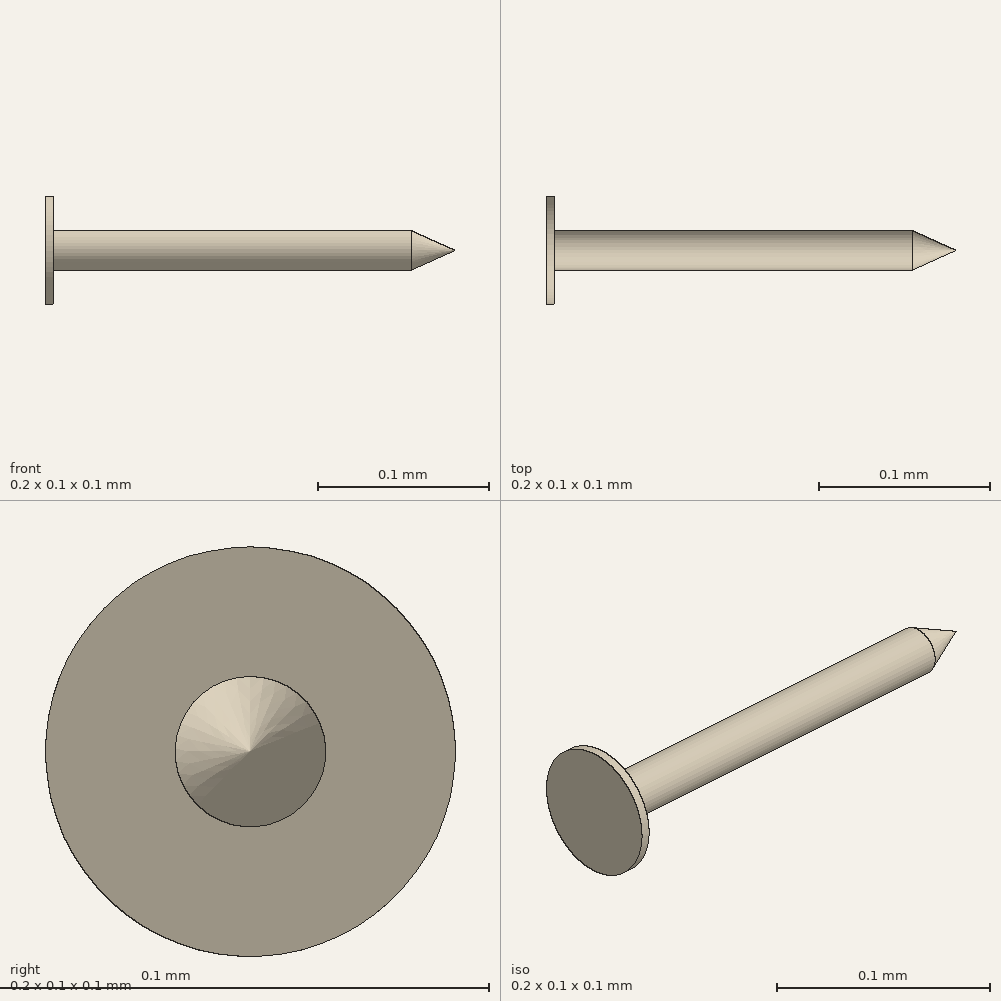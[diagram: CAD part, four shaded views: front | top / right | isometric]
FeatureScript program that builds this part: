
annotation { "Feature Type Name" : "Feature", "Feature Type Description" : "" }
export const myFeature = defineFeature(function(context is Context, id is Id, definition is map)
    precondition{}
    {
        {
            var Q0;
            Q0=qCreatedBy(makeId("Front.planeOp"),FACE);
            var sketch = newSketch(context, id + "F0", { "sketchPlane" : qUnion([Q0])});
            skLineSegment(sketch, "E0.bottom", {"start": v(-33.87, 35.93) * mm, "end": v(-33.66, 35.93) * mm});
            skLineSegment(sketch, "E0.top", {"start": v(-33.87, 35.92) * mm, "end": v(-33.66, 35.92) * mm});
            skLineSegment(sketch, "E0.left", {"start": v(-33.87, 35.93) * mm, "end": v(-33.87, 35.92) * mm});
            skLineSegment(sketch, "E0.right", {"start": v(-33.66, 35.93) * mm, "end": v(-33.66, 35.92) * mm});
            skLineSegment(sketch, "E1", {"start": v(-33.66, 35.93) * mm, "end": v(-33.64, 35.92) * mm});
            skLineSegment(sketch, "E2", {"start": v(-33.64, 35.92) * mm, "end": v(-33.66, 35.92) * mm});
            skLineSegment(sketch, "E3.bottom", {"start": v(-33.87, 35.92) * mm, "end": v(-33.88, 35.92) * mm});
            skLineSegment(sketch, "E3.top", {"start": v(-33.87, 35.95) * mm, "end": v(-33.88, 35.95) * mm});
            skLineSegment(sketch, "E3.left", {"start": v(-33.87, 35.92) * mm, "end": v(-33.87, 35.95) * mm});
            skLineSegment(sketch, "E3.right", {"start": v(-33.88, 35.92) * mm, "end": v(-33.88, 35.95) * mm});
            skSolve(sketch);
        }
        {
            var Q0;
            {var subQ3=sQuery(id+"F0.wireOp",EDGE,"E3.bottom");Q0=makeQuery(id+"F0.imprint","IMPRINT",FACE,{"disambiguationData":[TD([[makeQuery(id+"F0.imprint","IMPRINT",EDGE,{"derivedFrom":subQ3}),-1.0]])]});}
            var Q1;
            {var subQ0=sQuery(id+"F0.wireOp",EDGE,"E0.bottom");Q1=makeQuery(id+"F0.imprint","IMPRINT",FACE,{"disambiguationData":[TD([[makeQuery(id+"F0.imprint","IMPRINT",EDGE,{"derivedFrom":subQ0}),-1.0]])]});}
            var Q2;
            Q2=makeQuery(id+"F0.imprint","IMPRINT",FACE,{"disambiguationData":[TD([[makeQuery(id+"F0.imprint","IMPRINT",EDGE,{"derivedFrom":sQuery(id+"F0.wireOp",EDGE,"E0.right")}),1.0]])]});
            var Q3;
            Q3=sQuery(id+"F0.wireOp",EDGE,"E0.top");
            revolve(context, id + "F1", {"entities" : qUnion([Q0, Q1, Q2]), "axis" : qUnion([Q3]), "revolveType" : RevolveType.FULL});
        }
    });
